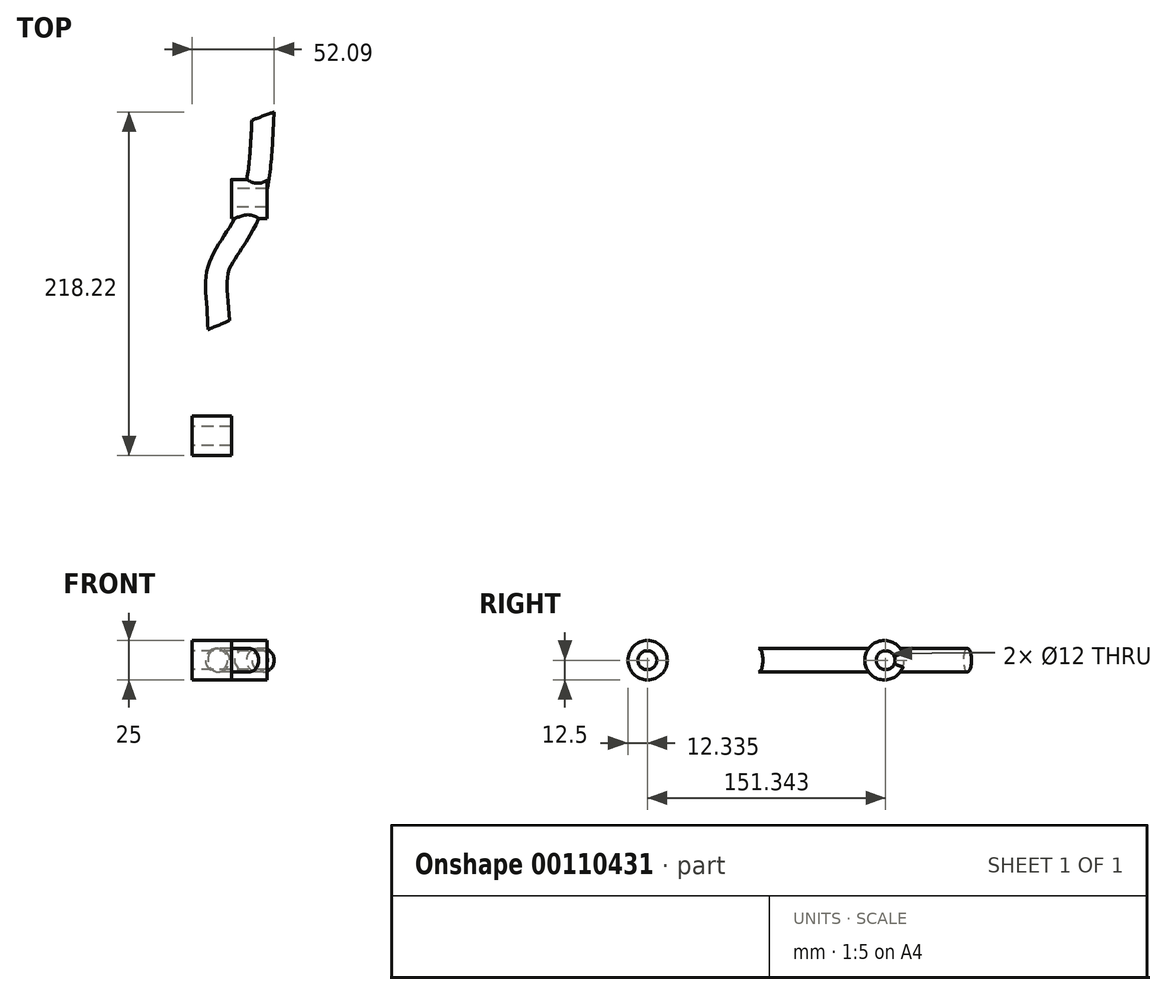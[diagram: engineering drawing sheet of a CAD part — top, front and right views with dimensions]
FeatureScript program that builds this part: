
annotation { "Feature Type Name" : "Feature", "Feature Type Description" : "" }
export const myFeature = defineFeature(function(context is Context, id is Id, definition is map)
    precondition{}
    {
        {
            var Q0;
            Q0=qCreatedBy(makeId("Front.planeOp"),FACE);
            var sketch = newSketch(context, id + "F0", { "sketchPlane" : qUnion([Q0])});
            skCircle(sketch, "E0", {"center": v(23.94, 0) * mm, "radius": 7.5 * mm});
            skSolve(sketch);
        }
        {
            var Q0;
            Q0=qCreatedBy(makeId("Right.planeOp"),FACE);
            var sketch = newSketch(context, id + "F1", { "sketchPlane" : qUnion([Q0])});
            skCircle(sketch, "E1", {"center": v(-142.24, 0) * mm, "radius": 12.5 * mm});
            skSolve(sketch);
        }
        {
            var Q0;
            Q0=qCreatedBy(makeId("Right.planeOp"),FACE);
            var sketch = newSketch(context, id + "F2", { "sketchPlane" : qUnion([Q0])});
            skCircle(sketch, "E2", {"center": v(-142.4, 0) * mm, "radius": 6 * mm});
            skCircle(sketch, "E3", {"center": v(8.94, 0) * mm, "radius": 6 * mm});
            skSolve(sketch);
        }
        {
            var Q0;
            Q0=qCreatedBy(makeId("Top.planeOp"),FACE);
            var sketch = newSketch(context, id + "F3", { "sketchPlane" : qUnion([Q0])});
            skPoint(sketch, "E4", {"position": v(0, -73.77) * mm});
            skPoint(sketch, "E5", {"position": v(28.06, 59.29) * mm});
            skFitSpline(sketch, "E6", {"points": [v(0, -73.77) * mm, v(0, -35.48) * mm, v(19.17, 0) * mm, v(28.06, 59.29) * mm], "startDerivative": vector(0, 142.96) * mm, "endDerivative": vector(8.65, 164.05) * mm});
            skSolve(sketch);
        }
        {
            var Q0;
            Q0 = qSketchRegion(id + "F0", true);
            var Q1;
            Q1=sQuery(id+"F3.wireOp",EDGE,"E6");
            sweep(context, id + "F4", {"profiles" : qUnion([Q0]), "path" : qUnion([Q1])});
        }
        {
            var Q0;
            Q0 = qSketchRegion(id + "F1", true);
            extrude(context, id + "F5", {"entities" : qUnion([Q0]), "operationType" : NewBodyOperationType.ADD, "endBound" : BoundingType.SYMMETRIC, "depth" : 25 * mm});
        }
        {
            var Q0;
            Q0=qCreatedBy(makeId("Right.planeOp"),FACE);
            var sketch = newSketch(context, id + "F6", { "sketchPlane" : qUnion([Q0])});
            skCircle(sketch, "E7", {"center": v(8.2, 0) * mm, "radius": 12.5 * mm});
            skSolve(sketch);
        }
        {
            var Q0;
            Q0 = qSketchRegion(id + "F6", true);
            extrude(context, id + "F7", {"entities" : qUnion([Q0]), "operationType" : NewBodyOperationType.ADD, "depth" : 35 * mm, "hasSecondDirection" : true, "secondDirectionOppositeDirection" : false, "secondDirectionDepth" : 12.5 * mm});
        }
        {
            var Q0;
            Q0 = qSketchRegion(id + "F2", true);
            extrude(context, id + "F8", {"entities" : qUnion([Q0]), "operationType" : NewBodyOperationType.REMOVE, "depth" : 50 * mm, "hasSecondDirection" : true, "secondDirectionOppositeDirection" : true, "secondDirectionDepth" : 25 * mm});
        }
    });
